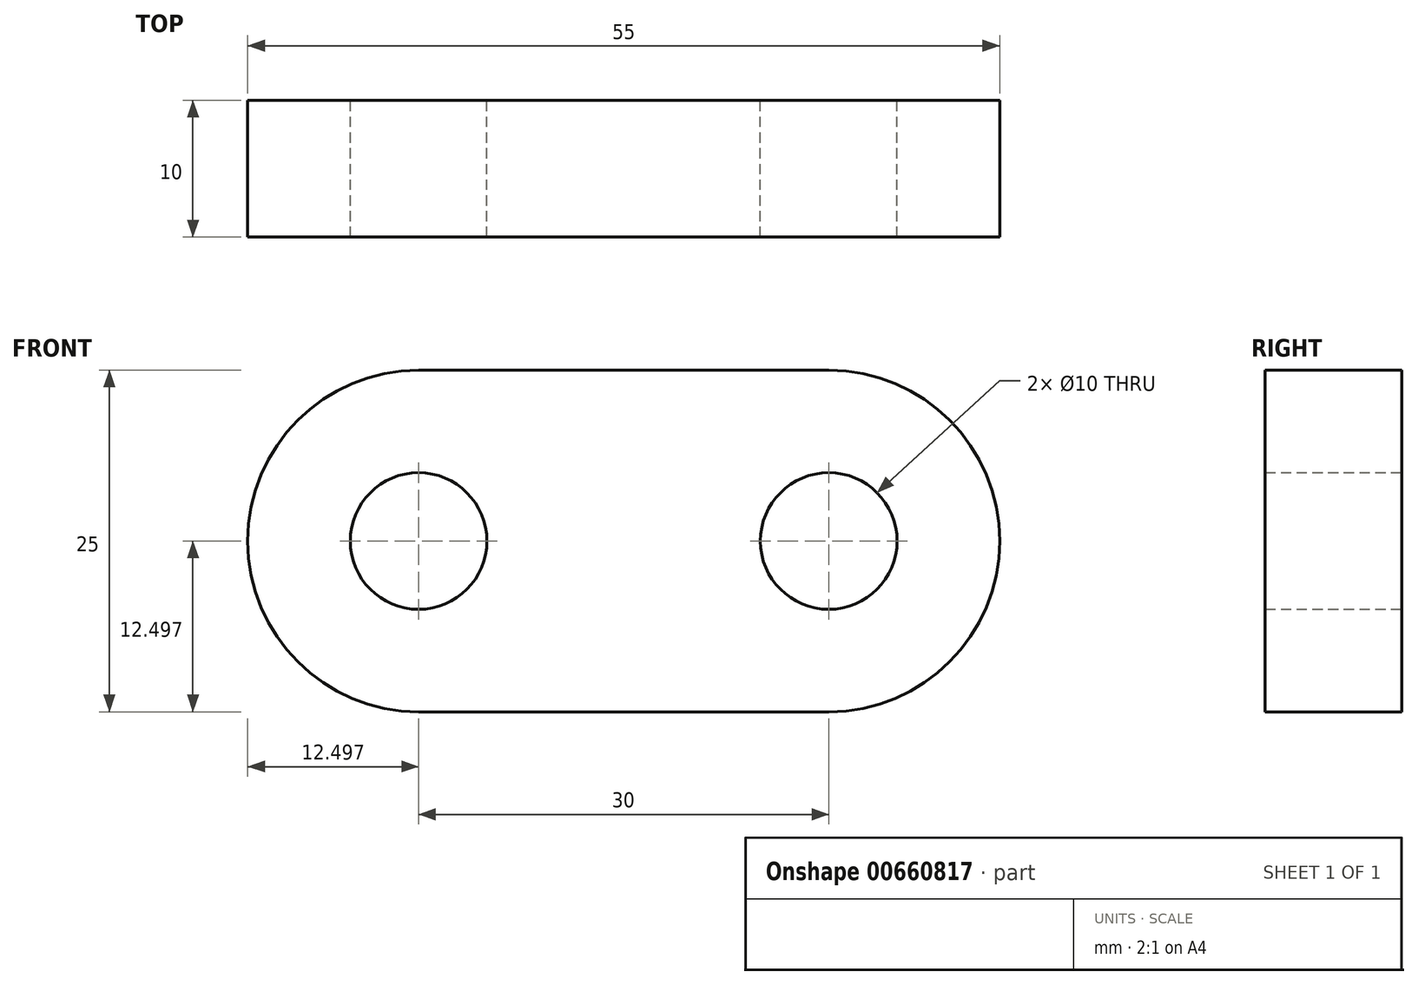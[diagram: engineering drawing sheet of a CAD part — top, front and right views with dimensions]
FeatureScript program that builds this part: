
annotation { "Feature Type Name" : "Feature", "Feature Type Description" : "" }
export const myFeature = defineFeature(function(context is Context, id is Id, definition is map)
    precondition{}
    {
        {
            var Q0;
            Q0=qCreatedBy(makeId("Front.planeOp"),FACE);
            var sketch = newSketch(context, id + "F0", { "sketchPlane" : qUnion([Q0])});
            skLineSegment(sketch, "E0.bottom", {"start": v(-12.82, 15.26) * mm, "end": v(17.18, 15.26) * mm});
            skLineSegment(sketch, "E0.top", {"start": v(-12.82, -9.74) * mm, "end": v(17.18, -9.74) * mm});
            skArc(sketch, "E1", {"start": v(-12.82, 15.26) * mm, "mid": v(-25.32, 2.76) * mm, "end": v(-12.82, -9.74) * mm});
            skArc(sketch, "E2", {"start": v(17.18, -9.74) * mm, "mid": v(29.68, 2.76) * mm, "end": v(17.18, 15.26) * mm});
            skCircle(sketch, "E3", {"center": v(17.18, 2.76) * mm, "radius": 5 * mm});
            skCircle(sketch, "E4", {"center": v(-12.82, 2.76) * mm, "radius": 5 * mm});
            skSolve(sketch);
        }
        {
            var Q0;
            Q0 = qSketchRegion(id + "F0", true);
            extrude(context, id + "F1", {"entities" : qUnion([Q0]), "depth" : 10 * mm, "offsetDistance" : 25.4 * mm});
        }
    });
